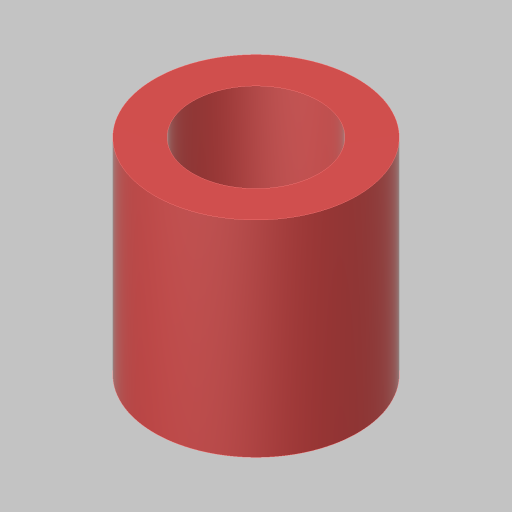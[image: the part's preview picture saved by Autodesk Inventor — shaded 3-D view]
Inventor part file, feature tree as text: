
AUTODESK INVENTOR PART (.ipt)
format: ipt  version: 2023.5 (Build 275446000, 446)  size: 101,376 bytes
history: native  units: in
note: dims shown in document units (in); Inventor stores cm internally (conversion verified against a paired STEP export)
features: extrude x1, sketch x1
ambient origin geometry x8: Origin, YZ Plane, XZ Plane, XY Plane, X Axis, Y Axis, Z Axis, Center Point
bodies: Solid1 (feature_tree)
feature tree (2):
  extrude  "Extrusion1"  Depth=0.67in
  sketch  "Sketch1"  dims[d0=0.41in d1=0.125in d2=0.67in d3=0.0in]
